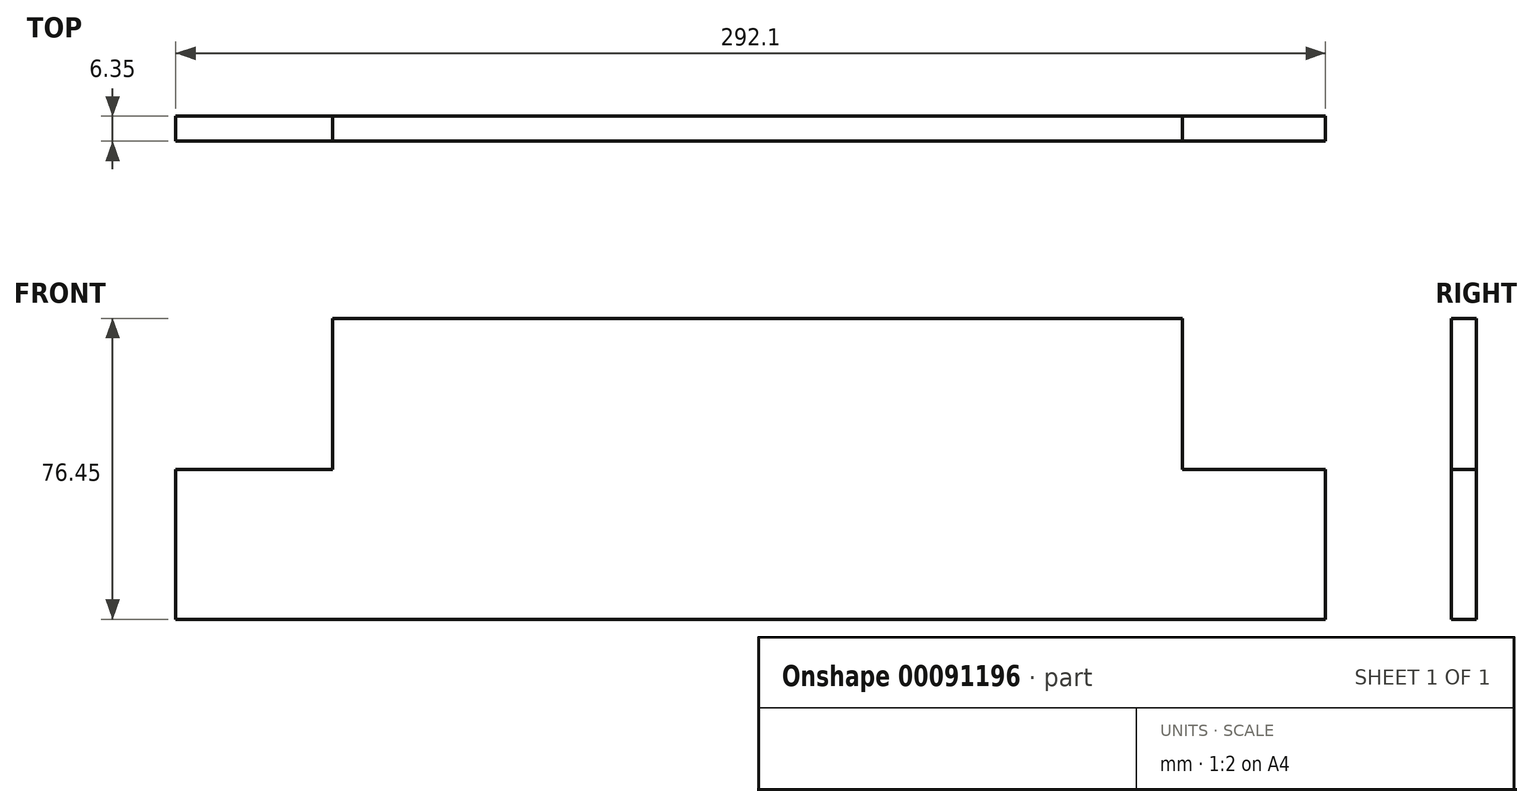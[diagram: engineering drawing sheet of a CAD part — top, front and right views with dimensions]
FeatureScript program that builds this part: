
annotation { "Feature Type Name" : "Feature", "Feature Type Description" : "" }
export const myFeature = defineFeature(function(context is Context, id is Id, definition is map)
    precondition{}
    {
        {
            var Q0;
            Q0=qCreatedBy(makeId("Front.planeOp"),FACE);
            var sketch = newSketch(context, id + "F0", { "sketchPlane" : qUnion([Q0])});
            skLineSegment(sketch, "E0.bottom", {"start": v(-103.94, 38.35) * mm, "end": v(111.96, 38.35) * mm});
            skLineSegment(sketch, "E0.top", {"start": v(-103.94, -37.85) * mm, "end": v(111.96, -37.85) * mm});
            skLineSegment(sketch, "E0.left", {"start": v(-103.94, 38.35) * mm, "end": v(-103.94, -37.85) * mm});
            skLineSegment(sketch, "E0.right", {"start": v(111.96, 38.35) * mm, "end": v(111.96, -37.85) * mm});
            skSolve(sketch);
        }
        {
            var Q0;
            Q0=makeQuery(id+"F0.imprint","IMPRINT",FACE,{"disambiguationData":[TD([[makeQuery(id+"F0.imprint","IMPRINT",EDGE,{"derivedFrom":sQuery(id+"F0.wireOp",EDGE,"E0.bottom")}),-1.0]])]});
            extrude(context, id + "F1", {"entities" : qUnion([Q0]), "depth" : 6.35 * mm});
        }
        {
            var Q0;
            Q0=makeQuery(id+"F1.opExtrude","CAP_FACE",FACE,{"disambiguationData":[OSD([sQuery(id+"F0.wireOp",EDGE,"E0.bottom"),sQuery(id+"F0.wireOp",EDGE,"E0.top"),sQuery(id+"F0.wireOp",EDGE,"E0.left"),sQuery(id+"F0.wireOp",EDGE,"E0.right")])],"isStart":false});
            var sketch = newSketch(context, id + "F2", { "sketchPlane" : qUnion([Q0])});
            skLineSegment(sketch, "E1.bottom", {"start": v(-143.75, 0) * mm, "end": v(148.35, 0) * mm});
            skLineSegment(sketch, "E1.top", {"start": v(-143.75, -38.1) * mm, "end": v(148.35, -38.1) * mm});
            skLineSegment(sketch, "E1.left", {"start": v(-143.75, 0) * mm, "end": v(-143.75, -38.1) * mm});
            skLineSegment(sketch, "E1.right", {"start": v(148.35, 0) * mm, "end": v(148.35, -38.1) * mm});
            skSolve(sketch);
        }
        {
            var Q0;
            Q0=makeQuery(id+"F2.imprint","IMPRINT",FACE,{"disambiguationData":[TD([[makeQuery(id+"F2.imprint","IMPRINT",EDGE,{"derivedFrom":sQuery(id+"F2.wireOp",EDGE,"E1.top")}),1.0]])]});
            extrude(context, id + "F3", {"entities" : qUnion([Q0]), "operationType" : NewBodyOperationType.ADD, "oppositeDirection" : true, "depth" : 6.35 * mm});
        }
    });
